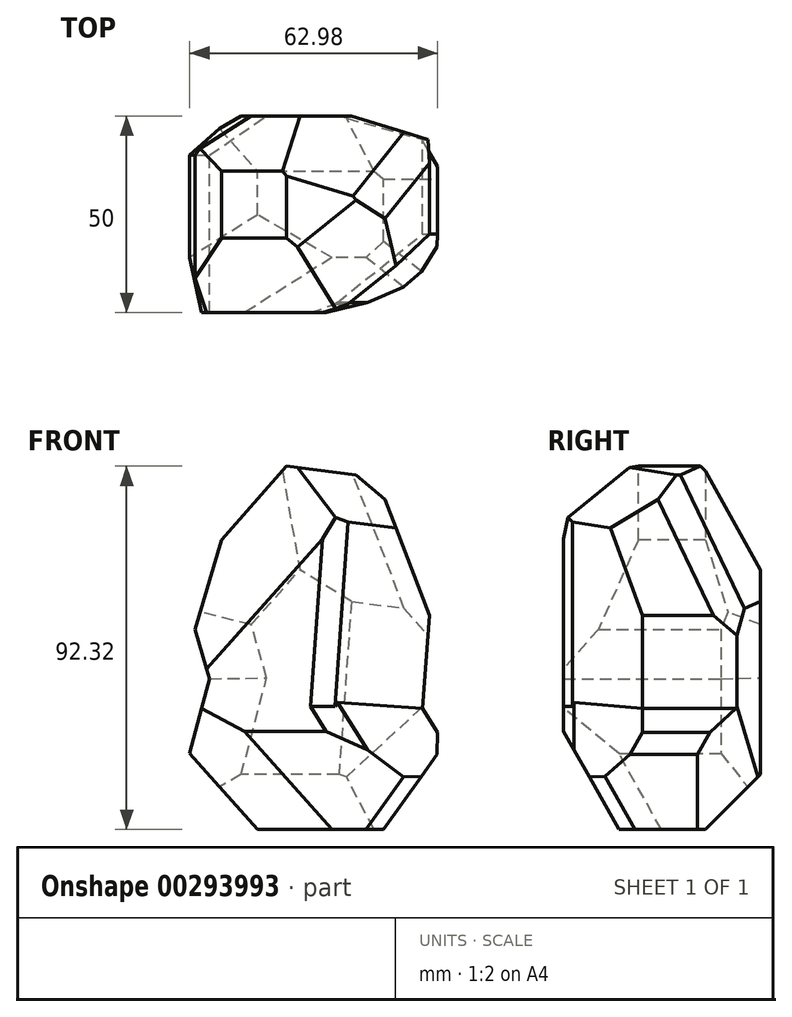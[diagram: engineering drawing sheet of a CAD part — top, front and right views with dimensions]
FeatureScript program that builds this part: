
annotation { "Feature Type Name" : "Feature", "Feature Type Description" : "" }
export const myFeature = defineFeature(function(context is Context, id is Id, definition is map)
    precondition{}
    {
        {
            var Q0;
            Q0=qCreatedBy(makeId("Front.planeOp"),FACE);
            var sketch = newSketch(context, id + "F0", { "sketchPlane" : qUnion([Q0])});
            skEllipse(sketch, "E0", {"center": v(0, 0) * mm, "majorRadius": 40 * mm, "minorRadius": 25 * mm, "majorAxis": v(0, 1), "construction": true});
            skLineSegment(sketch, "E1", {"start": v(0, -40) * mm, "end": v(-15.9, -40) * mm});
            skLineSegment(sketch, "E2", {"start": v(-15.9, -40) * mm, "end": v(-33.07, -20.66) * mm});
            skLineSegment(sketch, "E3", {"start": v(-33.07, -20.66) * mm, "end": v(-28.05, -1.66) * mm});
            skLineSegment(sketch, "E4", {"start": v(-28.05, -1.66) * mm, "end": v(-35.03, 22.41) * mm});
            skLineSegment(sketch, "E5", {"start": v(-35.03, 22.41) * mm, "end": v(-8.44, 52.32) * mm});
            skLineSegment(sketch, "E6", {"start": v(-8.44, 52.32) * mm, "end": v(14.42, 49.36) * mm});
            skLineSegment(sketch, "E7", {"start": v(14.42, 49.36) * mm, "end": v(27.78, 14.41) * mm});
            skLineSegment(sketch, "E8", {"start": v(27.78, 14.41) * mm, "end": v(26.08, -9.27) * mm});
            skLineSegment(sketch, "E9", {"start": v(26.08, -9.27) * mm, "end": v(31.73, -18.1) * mm});
            skLineSegment(sketch, "E10", {"start": v(31.73, -18.1) * mm, "end": v(16.13, -40) * mm});
            skLineSegment(sketch, "E11", {"start": v(16.13, -40) * mm, "end": v(-15.9, -40) * mm});
            skSolve(sketch);
        }
        {
            var Q0;
            Q0 = qSketchRegion(id + "F0", true);
            extrude(context, id + "F1", {"entities" : qUnion([Q0]), "depth" : 25 * mm, "hasSecondDirection" : true, "secondDirectionOppositeDirection" : true, "secondDirectionDepth" : 25 * mm});
        }
        {
            var Q0;
            Q0=makeQuery(id+"F1.opExtrude","CAP_EDGE",EDGE,{"disambiguationData":[OSD([sQuery(id+"F0.wireOp",EDGE,"E5")])],"isStart":false});
            chamfer(context, id + "F2", {"entities" : qUnion([Q0]), "width" : 19 * mm, "tangentPropagation" : true});
        }
        {
            var Q0;
            Q0=makeQuery(id+"F1.opExtrude","CAP_EDGE",EDGE,{"disambiguationData":[OSD([sQuery(id+"F0.wireOp",EDGE,"E8")])],"isStart":false});
            chamfer(context, id + "F3", {"entities" : qUnion([Q0]), "chamferType" : ChamferType.TWO_OFFSETS, "width1" : 20 * mm, "oppositeDirection" : false, "width2" : 25 * mm, "tangentPropagation" : true});
        }
        {
            var Q0;
            Q0=makeQuery(id+"F1.opExtrude","CAP_EDGE",EDGE,{"disambiguationData":[OSD([sQuery(id+"F0.wireOp",EDGE,"E9")])],"isStart":false});
            chamfer(context, id + "F4", {"entities" : qUnion([Q0]), "chamferType" : ChamferType.TWO_OFFSETS, "width1" : 20 * mm, "oppositeDirection" : false, "width2" : 20 * mm, "tangentPropagation" : true});
        }
        {
            var Q0;
            Q0=makeQuery(id+"F1.opExtrude","CAP_EDGE",EDGE,{"disambiguationData":[OSD([sQuery(id+"F0.wireOp",EDGE,"E10")])],"isStart":true});
            chamfer(context, id + "F5", {"entities" : qUnion([Q0]), "width" : 16 * mm, "tangentPropagation" : true});
        }
        {
            var Q0;
            Q0=makeQuery(id+"F1.opExtrude","SWEPT_EDGE",EDGE,{"disambiguationData":[OSD([sQuery(id+"F0.wireOp",EDGE,"E9"),sQuery(id+"F0.wireOp",EDGE,"E10")])]});
            chamfer(context, id + "F6", {"entities" : qUnion([Q0]), "width" : 5 * mm, "tangentPropagation" : true});
        }
        {
            var Q0;
            Q0=makeQuery(id+"F1.opExtrude","CAP_EDGE",EDGE,{"disambiguationData":[OSD([sQuery(id+"F0.wireOp",EDGE,"E8")])],"isStart":true});
            chamfer(context, id + "F7", {"entities" : qUnion([Q0]), "chamferType" : ChamferType.TWO_OFFSETS, "width1" : 20 * mm, "oppositeDirection" : false, "width2" : 6 * mm, "tangentPropagation" : true});
        }
        {
            var Q0;
            Q0=makeQuery(id+"F7.opChamfer","BLEND_EDGE",EDGE,{"blendedFrom":[makeQuery(id+"F1.opExtrude","CAP_EDGE",EDGE,{"disambiguationData":[OSD([sQuery(id+"F0.wireOp",EDGE,"E8")])],"isStart":true}),makeQuery(id+"F1.opExtrude","SWEPT_FACE",FACE,{"disambiguationData":[OSD([sQuery(id+"F0.wireOp",EDGE,"E6")])]})],"blendedInto":[makeQuery(id+"F1.opExtrude","SWEPT_FACE",FACE,{"disambiguationData":[OSD([sQuery(id+"F0.wireOp",EDGE,"E6")])]})]});
            chamfer(context, id + "F8", {"entities" : qUnion([Q0]), "chamferType" : ChamferType.TWO_OFFSETS, "width1" : 20 * mm, "oppositeDirection" : false, "width2" : 32 * mm, "tangentPropagation" : true});
        }
        {
            var Q0;
            Q0=makeQuery(id+"F1.opExtrude","CAP_EDGE",EDGE,{"disambiguationData":[OSD([sQuery(id+"F0.wireOp",EDGE,"E5")])],"isStart":true});
            chamfer(context, id + "F9", {"entities" : qUnion([Q0]), "chamferType" : ChamferType.TWO_OFFSETS, "width1" : 20 * mm, "oppositeDirection" : false, "width2" : 14 * mm, "tangentPropagation" : true});
        }
        {
            var Q0;
            Q0=makeQuery(id+"F1.opExtrude","CAP_EDGE",EDGE,{"disambiguationData":[OSD([sQuery(id+"F0.wireOp",EDGE,"E3")])],"isStart":true});
            var Q1;
            Q1=makeQuery(id+"F1.opExtrude","CAP_EDGE",EDGE,{"disambiguationData":[OSD([sQuery(id+"F0.wireOp",EDGE,"E4")])],"isStart":true});
            chamfer(context, id + "F10", {"entities" : qUnion([Q0, Q1]), "chamferType" : ChamferType.TWO_OFFSETS, "width1" : 14 * mm, "oppositeDirection" : false, "width2" : 10 * mm, "tangentPropagation" : true});
        }
        {
            var Q0;
            Q0=makeQuery(id+"F1.opExtrude","SWEPT_EDGE",EDGE,{"disambiguationData":[OSD([sQuery(id+"F0.wireOp",EDGE,"E4"),sQuery(id+"F0.wireOp",EDGE,"E5")])]});
            chamfer(context, id + "F11", {"entities" : qUnion([Q0]), "chamferType" : ChamferType.TWO_OFFSETS, "width1" : 12 * mm, "oppositeDirection" : false, "width2" : 15 * mm, "tangentPropagation" : true});
        }
        {
            var Q0;
            Q0=makeQuery(id+"F8.opChamfer","BLEND_EDGE",EDGE,{"blendedFrom":[makeQuery(id+"F7.opChamfer","BLEND_EDGE",EDGE,{"blendedFrom":[makeQuery(id+"F1.opExtrude","CAP_EDGE",EDGE,{"disambiguationData":[OSD([sQuery(id+"F0.wireOp",EDGE,"E8")])],"isStart":true}),makeQuery(id+"F1.opExtrude","SWEPT_FACE",FACE,{"disambiguationData":[OSD([sQuery(id+"F0.wireOp",EDGE,"E6")])]})],"blendedInto":[makeQuery(id+"F1.opExtrude","SWEPT_FACE",FACE,{"disambiguationData":[OSD([sQuery(id+"F0.wireOp",EDGE,"E6")])]})]}),makeQuery(id+"F1.opExtrude","SWEPT_FACE",FACE,{"disambiguationData":[OSD([sQuery(id+"F0.wireOp",EDGE,"E7")])]})],"blendedInto":[makeQuery(id+"F1.opExtrude","SWEPT_FACE",FACE,{"disambiguationData":[OSD([sQuery(id+"F0.wireOp",EDGE,"E7")])]})]});
            chamfer(context, id + "F12", {"entities" : qUnion([Q0]), "width" : 10 * mm, "tangentPropagation" : true});
        }
        {
            var Q0;
            Q0=makeQuery(id+"F3.opChamfer","BLEND_EDGE",EDGE,{"blendedFrom":[makeQuery(id+"F1.opExtrude","CAP_EDGE",EDGE,{"disambiguationData":[OSD([sQuery(id+"F0.wireOp",EDGE,"E8")])],"isStart":false}),makeQuery(id+"F1.opExtrude","SWEPT_FACE",FACE,{"disambiguationData":[OSD([sQuery(id+"F0.wireOp",EDGE,"E6")])]})],"blendedInto":[makeQuery(id+"F1.opExtrude","SWEPT_FACE",FACE,{"disambiguationData":[OSD([sQuery(id+"F0.wireOp",EDGE,"E6")])]})]});
            chamfer(context, id + "F13", {"entities" : qUnion([Q0]), "chamferType" : ChamferType.TWO_OFFSETS, "width1" : 20 * mm, "oppositeDirection" : false, "width2" : 12 * mm, "tangentPropagation" : true});
        }
        {
            var Q0;
            Q0=makeQuery(id+"F1.opExtrude","CAP_EDGE",EDGE,{"disambiguationData":[OSD([sQuery(id+"F0.wireOp",EDGE,"E11")])],"isStart":false});
            chamfer(context, id + "F14", {"entities" : qUnion([Q0]), "chamferType" : ChamferType.TWO_OFFSETS, "width1" : 14 * mm, "oppositeDirection" : false, "width2" : 25 * mm, "tangentPropagation" : true});
        }
        {
            var Q0;
            Q0=makeQuery(id+"F1.opExtrude","CAP_EDGE",EDGE,{"disambiguationData":[OSD([sQuery(id+"F0.wireOp",EDGE,"E11")])],"isStart":true});
            chamfer(context, id + "F15", {"entities" : qUnion([Q0]), "chamferType" : ChamferType.TWO_OFFSETS, "width1" : 14 * mm, "oppositeDirection" : false, "width2" : 14 * mm, "tangentPropagation" : true});
        }
        {
            var Q0;
            Q0=makeQuery(id+"F14.opChamfer","BLEND_EDGE",EDGE,{"blendedFrom":[makeQuery(id+"F1.opExtrude","CAP_EDGE",EDGE,{"disambiguationData":[OSD([sQuery(id+"F0.wireOp",EDGE,"E11")])],"isStart":false}),makeQuery(id+"F1.opExtrude","SWEPT_FACE",FACE,{"disambiguationData":[OSD([sQuery(id+"F0.wireOp",EDGE,"E2")])]})],"blendedInto":[makeQuery(id+"F1.opExtrude","SWEPT_FACE",FACE,{"disambiguationData":[OSD([sQuery(id+"F0.wireOp",EDGE,"E2")])]})]});
            chamfer(context, id + "F16", {"entities" : qUnion([Q0]), "chamferType" : ChamferType.TWO_OFFSETS, "width1" : 10 * mm, "oppositeDirection" : false, "width2" : 15 * mm, "tangentPropagation" : true});
        }
        {
            var Q0;
            Q0=makeQuery(id+"F14.opChamfer","BLEND_EDGE",EDGE,{"blendedFrom":[makeQuery(id+"F1.opExtrude","CAP_EDGE",EDGE,{"disambiguationData":[OSD([sQuery(id+"F0.wireOp",EDGE,"E11")])],"isStart":false}),makeQuery(id+"F1.opExtrude","SWEPT_FACE",FACE,{"disambiguationData":[OSD([sQuery(id+"F0.wireOp",EDGE,"E10")])]})],"blendedInto":[makeQuery(id+"F1.opExtrude","SWEPT_FACE",FACE,{"disambiguationData":[OSD([sQuery(id+"F0.wireOp",EDGE,"E10")])]})]});
            chamfer(context, id + "F17", {"entities" : qUnion([Q0]), "width" : 5 * mm, "tangentPropagation" : true});
        }
        {
            var Q0;
            {var subQ0=sQuery(id+"F0.wireOp",EDGE,"E8");Q0=makeQuery(id+"F3.opChamfer","BLEND_EDGE",EDGE,{"blendedFrom":[makeQuery(id+"F1.opExtrude","CAP_EDGE",EDGE,{"disambiguationData":[OSD([subQ0])],"isStart":false}),makeQuery(id+"F1.opExtrude","CAP_FACE",FACE,{"disambiguationData":[OSD([sQuery(id+"F0.wireOp",EDGE,"E2"),sQuery(id+"F0.wireOp",EDGE,"E3"),sQuery(id+"F0.wireOp",EDGE,"E4"),sQuery(id+"F0.wireOp",EDGE,"E5"),sQuery(id+"F0.wireOp",EDGE,"E6"),sQuery(id+"F0.wireOp",EDGE,"E7"),subQ0,sQuery(id+"F0.wireOp",EDGE,"E9"),sQuery(id+"F0.wireOp",EDGE,"E10"),sQuery(id+"F0.wireOp",EDGE,"E11")])],"isStart":false})],"blendedInto":[makeQuery(id+"F1.opExtrude","CAP_FACE",FACE,{"disambiguationData":[OSD([sQuery(id+"F0.wireOp",EDGE,"E2"),sQuery(id+"F0.wireOp",EDGE,"E3"),sQuery(id+"F0.wireOp",EDGE,"E4"),sQuery(id+"F0.wireOp",EDGE,"E5"),sQuery(id+"F0.wireOp",EDGE,"E6"),sQuery(id+"F0.wireOp",EDGE,"E7"),subQ0,sQuery(id+"F0.wireOp",EDGE,"E9"),sQuery(id+"F0.wireOp",EDGE,"E10"),sQuery(id+"F0.wireOp",EDGE,"E11")])],"isStart":false})]});}
            chamfer(context, id + "F18", {"entities" : qUnion([Q0]), "width" : 10 * mm, "tangentPropagation" : true});
        }
        {
            var Q0;
            {var subQ0=sQuery(id+"F0.wireOp",EDGE,"E9");Q0=makeQuery(id+"F4.opChamfer","BLEND_EDGE",EDGE,{"blendedFrom":[makeQuery(id+"F1.opExtrude","CAP_EDGE",EDGE,{"disambiguationData":[OSD([subQ0])],"isStart":false}),makeQuery(id+"F1.opExtrude","CAP_FACE",FACE,{"disambiguationData":[OSD([sQuery(id+"F0.wireOp",EDGE,"E2"),sQuery(id+"F0.wireOp",EDGE,"E3"),sQuery(id+"F0.wireOp",EDGE,"E4"),sQuery(id+"F0.wireOp",EDGE,"E5"),sQuery(id+"F0.wireOp",EDGE,"E6"),sQuery(id+"F0.wireOp",EDGE,"E7"),sQuery(id+"F0.wireOp",EDGE,"E8"),subQ0,sQuery(id+"F0.wireOp",EDGE,"E10"),sQuery(id+"F0.wireOp",EDGE,"E11")])],"isStart":false})],"blendedInto":[makeQuery(id+"F1.opExtrude","CAP_FACE",FACE,{"disambiguationData":[OSD([sQuery(id+"F0.wireOp",EDGE,"E2"),sQuery(id+"F0.wireOp",EDGE,"E3"),sQuery(id+"F0.wireOp",EDGE,"E4"),sQuery(id+"F0.wireOp",EDGE,"E5"),sQuery(id+"F0.wireOp",EDGE,"E6"),sQuery(id+"F0.wireOp",EDGE,"E7"),sQuery(id+"F0.wireOp",EDGE,"E8"),subQ0,sQuery(id+"F0.wireOp",EDGE,"E10"),sQuery(id+"F0.wireOp",EDGE,"E11")])],"isStart":false})]});}
            chamfer(context, id + "F19", {"entities" : qUnion([Q0]), "width" : 9 * mm, "tangentPropagation" : true});
        }
    });
